# Revit family: 55-9791-Z5-CL
name_source: partatom
category: Luminarias
revit_build: Autodesk Revit 2017 (Build: 20160225_1515(x64)
units: mm (PartAtom-declared; Revit-internal decimal feet)

## family parameters
Compartido = Sí
Corte con vacíos al cargar = No
Cota de conector redondo = Diámetro de uso
Número OmniClass = 23.80.70.00
Origen de luz = No
Punto de cálculo de habitación = No
Se basa en plano de trabajo = No
Siempre vertical = Sí
Tipo de pieza = Normal
Título OmniClass = Lighting

## types (1)
- 55-9791-Z5-CL
    Acabado = Gris urbano, Transparente, Mate
    CRI = 80
    Catálogo = Outdoor
    CodigoGubimclass = 50.60.50.20
    CodigoOmniclass = 21-04 50 40
    CodigoUniclass2015 = EF_70_80
    CodigoUniformat2010 = D5040
    DescripcionGubimclass = Iluminación interior
    DescripcionOmniclass = Lighting
    DescripcionUniclass2015 = Lighting
    DescripcionUniformat2010 = Lighting
    EAN13 = 8435381459017
    Eficiencia energética = LED A++
    Etiqueta V/f = 100-240V/50-60Hz
    Fabricante = LEDS C4
    Familia = Newton LED 800mm
    FechaVersion = Julio 2020
    Ficha = http://files.leds-c4.com
    Fotometría = http://files.leds-c4.com
    Fuente de luz = 48xLED 12.7 1361.00 lm
    IK = IK08
    IMC = http://files.leds-c4.com
    IP = IP65
    IfcExportAs = IfcLightFixture
    IfcExportType = NOTDEFINED
    Imagen web = http://files.leds-c4.com
    LDT = http://files.leds-c4.com
    Lumenes reales (lm) = 573
    Material = Aluminio, Policarbonato
    Peso neto (KG) = 4.35
    Pluma comercial = http://files.leds-c4.com
    Producto descatalogado = Catalogado ES
    Rayo de luz = Check Photometric file
    Referencia = 55-9791-Z5-CL
    Temperatura color led (K) = Blanco cálido - 3000K
    Tender text (Castellano) = LEDS C4
Newton LED 800mm
55-9791-Z5-CLV2

Baliza de uso exterior para iluminar hacia abajo. 
Material estructura: Aluminio. Acabado estructura: Gris urbano. Material difusor: Policarbonato. Acabado difusor: Transparente, Mate. Protección contra los rayos ultravioleta. Garantía: 5 Años.

Peso neto del producto (Kg): 4.350
Anchura o diámetro del producto (mm): 160
Altura del producto (mm): 800

Clase 1. IP: IP65. IK: IK08. LED. Nº de portalámparas o Leds: 48. Marca del LED: HANGKE. Marca del Driver: EAGLERISE. Potencia máxima de la fuente de luz: 12.7W. Temperatura de color: Blanco cálido - 3000K. Índice de reproducción cromática: 80. Steps Mac Adam: 3. Diámetro máximo de la bombilla que admite la luminaria: 50.000h L80B20. UGR:  19.9. Riesgo fotobiológico: RG0. Flujo real (lm): 573. Flujo nominal (lm): 1361. Lm/W reales: 41. Rango de voltaje/frecuencia: 100-240/50-60Hz. Voltaje: 3. Equipo incluido: Si, electrónico. Equipo multivoltaje incluido. Potencia total: 13.9. Factor de potencia: 0.90.
    Tender text (English) = LEDS C4
Newton LED 800mm
55-9791-Z5-CLV2

Bollard for outdoor use. 

For downlighting. Structure material: Aluminium. Structure finish: Urban grey. Diffuser material: Polycarbonate. Diffuser finish: Transparent, Matt. UV protection. Warranty: 5 Years.

Product net weight (Kg): 4.350
Product width or diameter (mm): 160
Product height (mm): 800

Class 1. IP: IP65. IK: IK08. LED. No. of lampholders or LEDs: 48. LED brand: HANGKE. Driver brand: EAGLERISE. Maximum power of light source: 12.7W. Colour temperature: LED warm-white 3000K. Colour rendering index: 80. MacAdam Steps: 3. Maximum diameter of luminaire bulb: 50.000h L80B20. UGR:  19.9. Photobiological risk: RG0. Real flux (lm): 573. Nominal flux (lm): 1361. Lm/Real W: 41. Voltage and frequency range: 100-240/50-60Hz. Voltage: 3. Gear included: Yes, electronic. Multi-voltage gear included. Total power: 13.9. Power factor: 0.90.
    Tipo = Baliza
    Vatios (W) = 13.9
    Versión = v1
